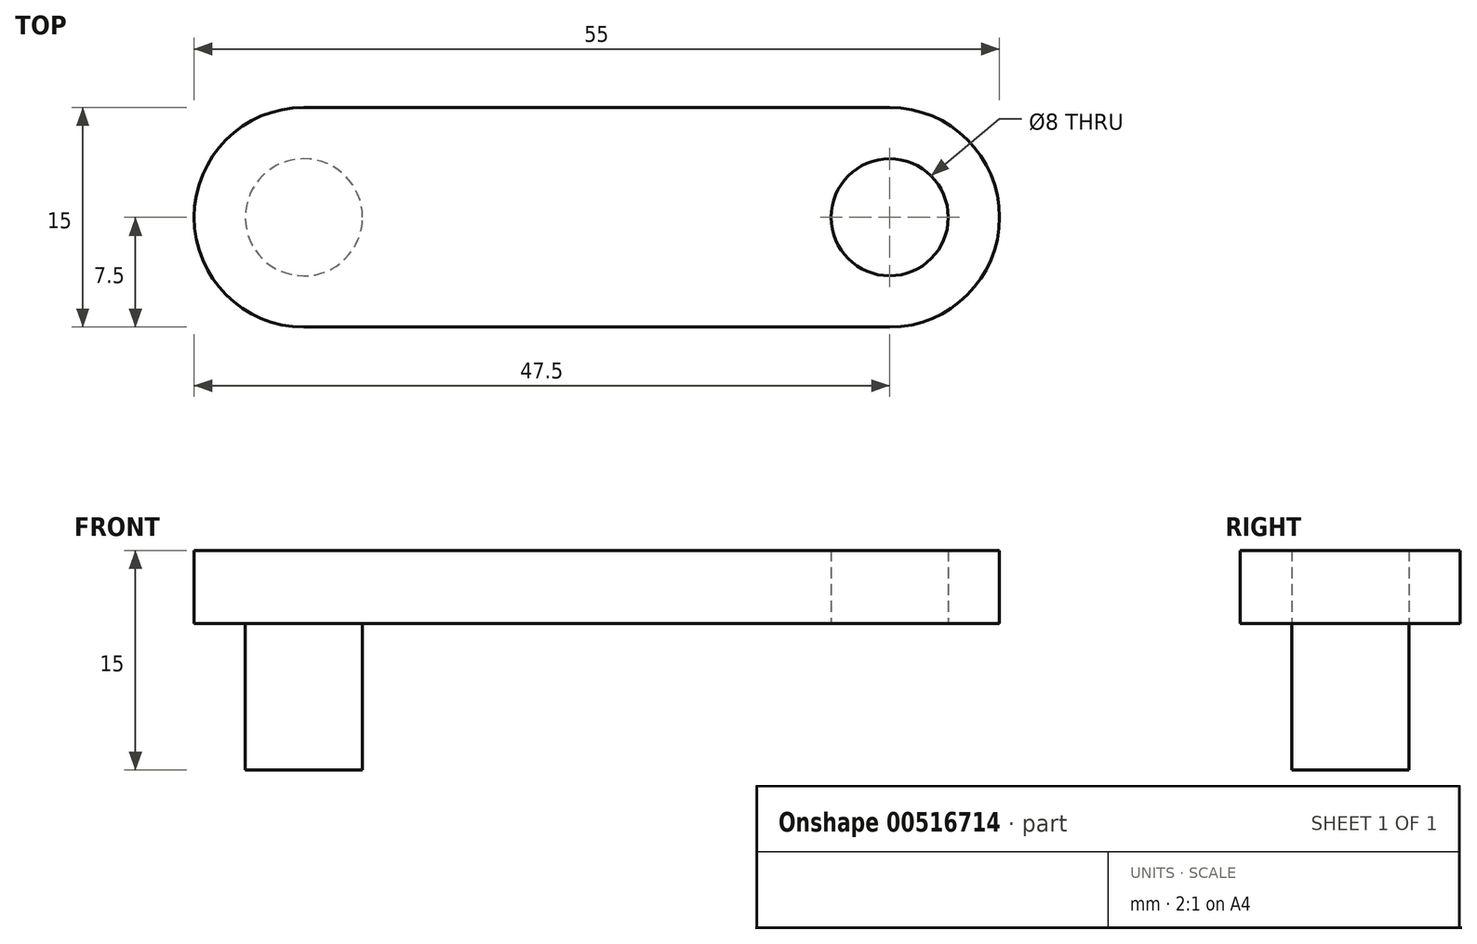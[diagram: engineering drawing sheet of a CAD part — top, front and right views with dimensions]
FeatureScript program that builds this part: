
annotation { "Feature Type Name" : "Feature", "Feature Type Description" : "" }
export const myFeature = defineFeature(function(context is Context, id is Id, definition is map)
    precondition{}
    {
        {
            var Q0;
            Q0=qCreatedBy(makeId("Top.planeOp"),FACE);
            var sketch = newSketch(context, id + "F0", { "sketchPlane" : qUnion([Q0])});
            skLineSegment(sketch, "E0.bottom", {"start": v(20, 7.5) * mm, "end": v(-20, 7.5) * mm});
            skLineSegment(sketch, "E0.top", {"start": v(20, -7.5) * mm, "end": v(-20, -7.5) * mm});
            skPoint(sketch, "E0.middle", {"position": v(0, 0) * mm});
            skArc(sketch, "E1", {"start": v(-20, 7.5) * mm, "mid": v(-27.5, 0) * mm, "end": v(-20, -7.5) * mm});
            skCircle(sketch, "E2", {"center": v(-20, 0) * mm, "radius": 4 * mm});
            skCircle(sketch, "E3", {"center": v(20, 0) * mm, "radius": 4 * mm});
            skArc(sketch, "E4", {"start": v(20, -7.5) * mm, "mid": v(27.5, 0) * mm, "end": v(20, 7.5) * mm});
            skSolve(sketch);
        }
        {
            var Q0;
            Q0=makeQuery(id+"F0.imprint","IMPRINT",FACE,{"disambiguationData":[TD([[makeQuery(id+"F0.imprint","IMPRINT",EDGE,{"derivedFrom":sQuery(id+"F0.wireOp",EDGE,"E0.bottom")}),1.0]])]});
            extrude(context, id + "F1", {"entities" : qUnion([Q0]), "endBound" : BoundingType.SYMMETRIC, "depth" : 5 * mm, "offsetDistance" : 25.4 * mm});
        }
        {
            var Q0;
            Q0=makeQuery(id+"F1.opExtrude","CAP_FACE",FACE,{"disambiguationData":[OSD([sQuery(id+"F0.wireOp",EDGE,"E0.bottom"),sQuery(id+"F0.wireOp",EDGE,"E0.top"),sQuery(id+"F0.wireOp",EDGE,"E1"),sQuery(id+"F0.wireOp",EDGE,"E2"),sQuery(id+"F0.wireOp",EDGE,"E3"),sQuery(id+"F0.wireOp",EDGE,"E4")])],"isStart":false});
            var sketch = newSketch(context, id + "F2", { "sketchPlane" : qUnion([Q0])});
            skCircle(sketch, "E5", {"center": v(-20, 0) * mm, "radius": 4 * mm});
            skSolve(sketch);
        }
        {
            var Q0;
            Q0 = qSketchRegion(id + "F2", true);
            extrude(context, id + "F3", {"entities" : qUnion([Q0]), "operationType" : NewBodyOperationType.ADD, "oppositeDirection" : true, "depth" : 15 * mm, "offsetDistance" : 25.4 * mm});
        }
    });
